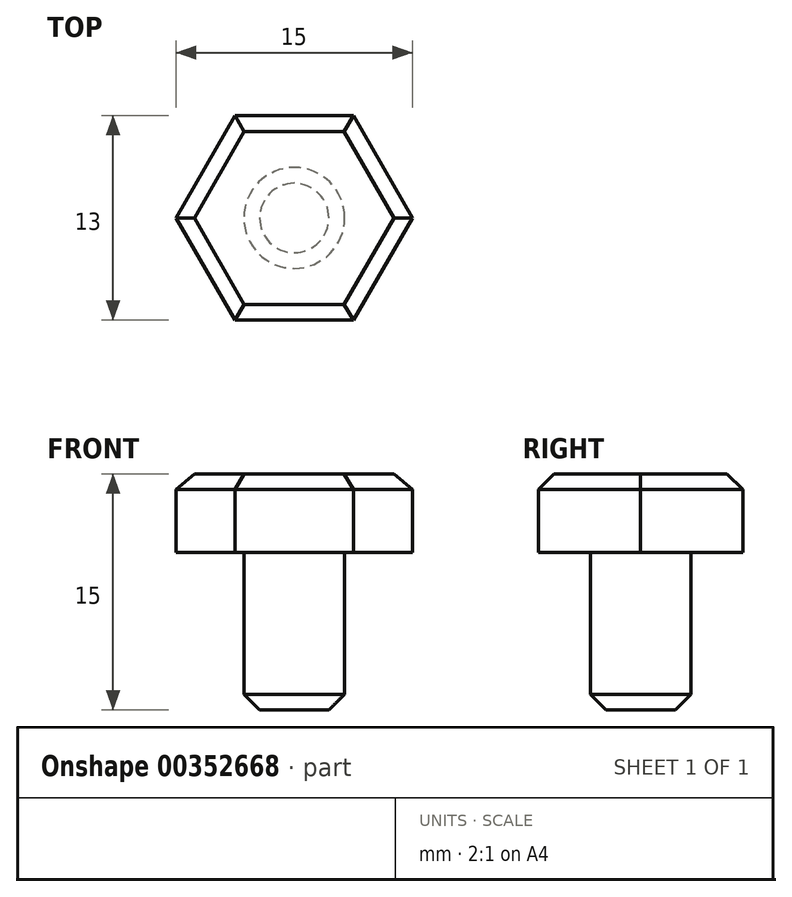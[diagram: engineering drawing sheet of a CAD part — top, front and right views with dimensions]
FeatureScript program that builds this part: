
annotation { "Feature Type Name" : "Feature", "Feature Type Description" : "" }
export const myFeature = defineFeature(function(context is Context, id is Id, definition is map)
    precondition{}
    {
        {
            var Q0;
            Q0=qCreatedBy(makeId("Top.planeOp"),FACE);
            var sketch = newSketch(context, id + "F0", { "sketchPlane" : qUnion([Q0])});
            skCircle(sketch, "E0", {"center": v(0, 0) * mm, "radius": 3.2 * mm});
            skSolve(sketch);
        }
        {
            var Q0;
            Q0=makeQuery(id+"F0.imprint","IMPRINT",FACE,{"disambiguationData":[TD([[makeQuery(id+"F0.imprint","IMPRINT",EDGE,{"derivedFrom":sQuery(id+"F0.wireOp",EDGE,"E0")}),1.0]])]});
            extrude(context, id + "F1", {"entities" : qUnion([Q0]), "depth" : 10 * mm});
        }
        {
            var Q0;
            Q0=makeQuery(id+"F1.opExtrude","CAP_FACE",FACE,{"disambiguationData":[OSD([sQuery(id+"F0.wireOp",EDGE,"E0")])],"isStart":false});
            var sketch = newSketch(context, id + "F2", { "sketchPlane" : qUnion([Q0])});
            skCircle(sketch, "E1.cCircle", {"center": v(0, 0) * mm, "radius": 7.5 * mm, "construction": true});
            skLineSegment(sketch, "E1.0", {"start": v(7.5, 0) * mm, "end": v(3.75, -6.5) * mm});
            skLineSegment(sketch, "E1.1", {"start": v(3.75, -6.5) * mm, "end": v(-3.75, -6.5) * mm});
            skLineSegment(sketch, "E1.2", {"start": v(-3.75, -6.5) * mm, "end": v(-7.5, 0) * mm});
            skLineSegment(sketch, "E1.3", {"start": v(-7.5, 0) * mm, "end": v(-3.75, 6.5) * mm});
            skLineSegment(sketch, "E1.4", {"start": v(-3.75, 6.5) * mm, "end": v(3.75, 6.5) * mm});
            skLineSegment(sketch, "E1.5", {"start": v(3.75, 6.5) * mm, "end": v(7.5, 0) * mm});
            skSolve(sketch);
        }
        {
            var Q0;
            Q0=makeQuery(id+"F2.imprint","IMPRINT",FACE,{"disambiguationData":[TD([[makeQuery(id+"F2.imprint","IMPRINT",EDGE,{"derivedFrom":sQuery(id+"F2.wireOp",EDGE,"E1.0")}),-1.0]])]});
            var Q1;
            Q1=makeQuery(id+"F2.imprint","IMPRINT",FACE,{"disambiguationData":[TD([[makeQuery(id+"F2.imprint","IMPRINT",EDGE,{"derivedFrom":makeQuery(id+"F1.opExtrude","CAP_EDGE",EDGE,{"disambiguationData":[OSD([sQuery(id+"F0.wireOp",EDGE,"E0")])],"isStart":false})}),1.0]])]});
            extrude(context, id + "F3", {"entities" : qUnion([Q0, Q1]), "operationType" : NewBodyOperationType.ADD, "depth" : 5 * mm});
        }
        {
            var Q0;
            Q0=makeQuery(id+"F3.opExtrude","CAP_FACE",FACE,{"disambiguationData":[OSD([sQuery(id+"F2.wireOp",EDGE,"E1.0"),sQuery(id+"F2.wireOp",EDGE,"E1.1"),sQuery(id+"F2.wireOp",EDGE,"E1.2"),sQuery(id+"F2.wireOp",EDGE,"E1.3"),sQuery(id+"F2.wireOp",EDGE,"E1.4"),sQuery(id+"F2.wireOp",EDGE,"E1.5")])],"isStart":false});
            var Q1;
            Q1=makeQuery(id+"F1.opExtrude","CAP_EDGE",EDGE,{"disambiguationData":[OSD([sQuery(id+"F0.wireOp",EDGE,"E0")])],"isStart":true});
            chamfer(context, id + "F4", {"entities" : qUnion([Q0, Q1]), "width" : 1 * mm, "tangentPropagation" : true});
        }
    });
